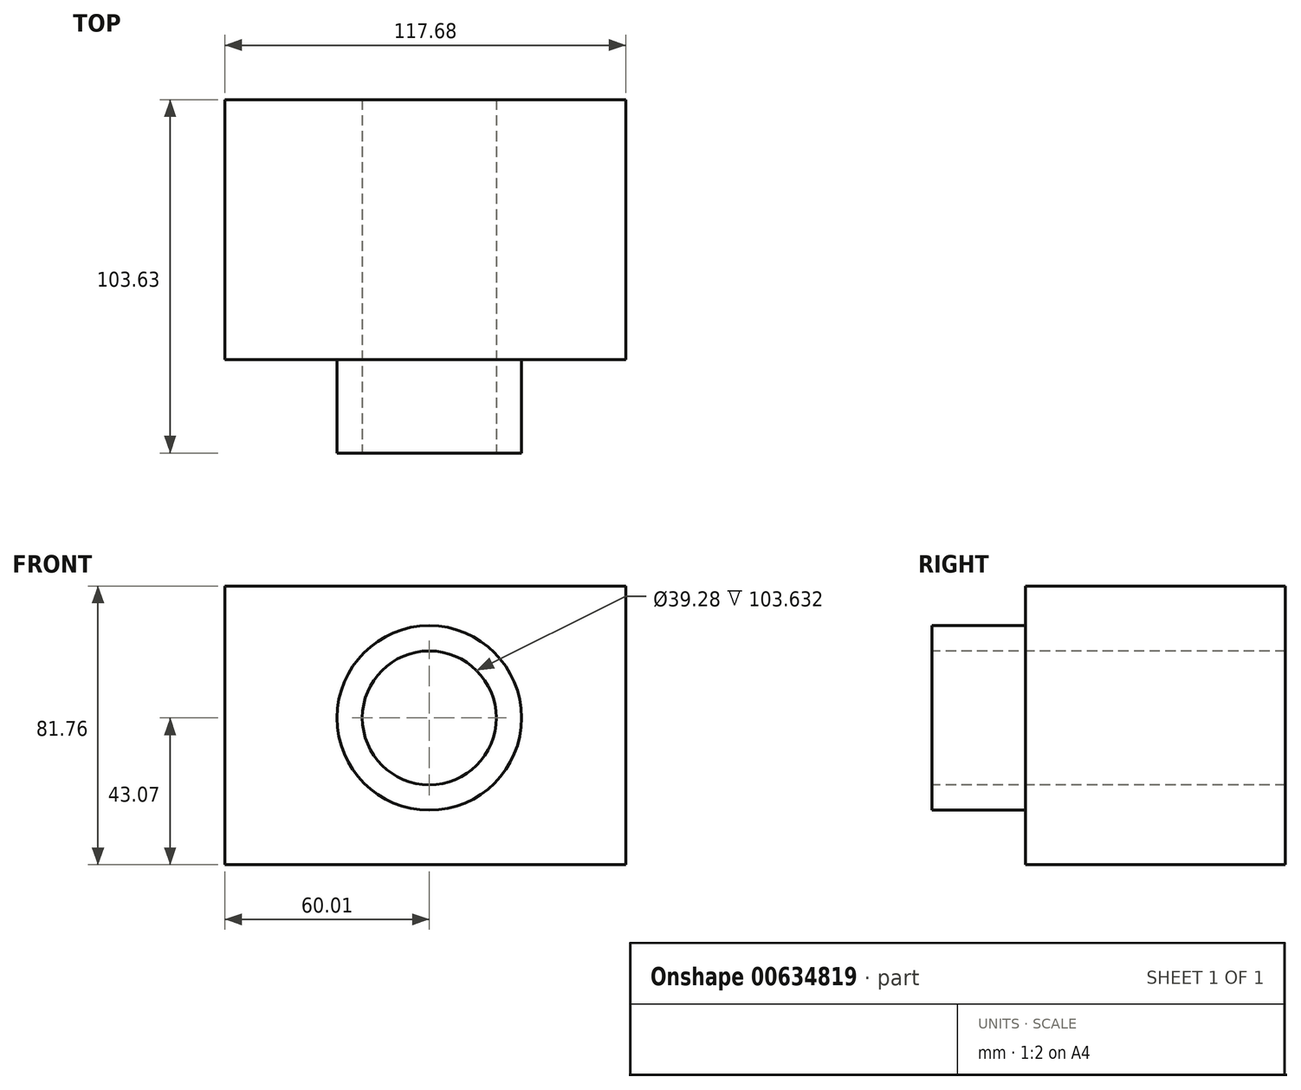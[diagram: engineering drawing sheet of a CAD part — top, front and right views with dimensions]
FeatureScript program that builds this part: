
annotation { "Feature Type Name" : "Feature", "Feature Type Description" : "" }
export const myFeature = defineFeature(function(context is Context, id is Id, definition is map)
    precondition{}
    {
        {
            var Q0;
            Q0=qCreatedBy(makeId("Front.planeOp"),FACE);
            var sketch = newSketch(context, id + "F0", { "sketchPlane" : qUnion([Q0])});
            skLineSegment(sketch, "E0", {"start": v(-60, 38.7) * mm, "end": v(57.67, 38.7) * mm});
            skLineSegment(sketch, "E1", {"start": v(57.67, 38.7) * mm, "end": v(57.67, -43.07) * mm});
            skLineSegment(sketch, "E2", {"start": v(57.67, -43.07) * mm, "end": v(57.67, 35.19) * mm});
            skLineSegment(sketch, "E3", {"start": v(57.67, 35.19) * mm, "end": v(57.67, 38.7) * mm});
            skLineSegment(sketch, "E4", {"start": v(-60, 38.7) * mm, "end": v(-60, -43.07) * mm});
            skLineSegment(sketch, "E5", {"start": v(-60, -43.07) * mm, "end": v(57.67, -43.07) * mm});
            skSolve(sketch);
        }
        {
            var Q0;
            Q0 = qSketchRegion(id + "F0", true);
            extrude(context, id + "F1", {"entities" : qUnion([Q0]), "oppositeDirection" : true, "depth" : 76.2 * mm, "offsetDistance" : 25.4 * mm});
        }
        {
            var Q0;
            Q0=qCreatedBy(makeId("Front.planeOp"),FACE);
            var sketch = newSketch(context, id + "F2", { "sketchPlane" : qUnion([Q0])});
            skCircle(sketch, "E6", {"center": v(0, 0) * mm, "radius": 27.06 * mm});
            skSolve(sketch);
        }
        {
            var Q0;
            Q0 = qSketchRegion(id + "F2", true);
            extrude(context, id + "F3", {"entities" : qUnion([Q0]), "operationType" : NewBodyOperationType.ADD, "depth" : 27.43 * mm, "offsetDistance" : 25.4 * mm});
        }
        {
            var Q0;
            Q0=makeQuery(id+"F3.opExtrude","CAP_FACE",FACE,{"disambiguationData":[OSD([sQuery(id+"F2.wireOp",EDGE,"E6")])],"isStart":false});
            var sketch = newSketch(context, id + "F4", { "sketchPlane" : qUnion([Q0])});
            skCircle(sketch, "E7", {"center": v(0, 0) * mm, "radius": 19.64 * mm});
            skSolve(sketch);
        }
        {
            var Q0;
            Q0 = qSketchRegion(id + "F4", true);
            extrude(context, id + "F5", {"entities" : qUnion([Q0]), "operationType" : NewBodyOperationType.REMOVE, "oppositeDirection" : true, "depth" : 197.1 * mm, "offsetDistance" : 25.4 * mm});
        }
    });
